# Revit family: Distributeur
name_source: partatom
category: Furniture
units: mm (PartAtom-declared; Revit-internal decimal feet)

## family parameters
Cut with Voids When Loaded = No
Host = Face
Room Calculation Point = No
Shared = No

## types (1)
- Distributeur
    Adresse = ZI de Chapotin BP 6 69970 Chaponnay FRANCE
    BIM object by Polantis = http://www.polantis.com
    Default Elevation = 100 cm
    Description = Fabricant Français d'Accessoires Sanitaires pour Collectivites, PELLET ASC a developpe des gammes specialisees pour ameliorer le Confort et la Securite de 

la salle de bain au quotidien.
    Fax. = 04.78.96.70.52
    Manufacturer = Pellet ASC
    Model = 003511 Distributeur papier WC en laiton nickelchrom- 152 96 68 mm avec rouleau bois18 mm
    Telephone = 04.78.96.82.20
    Type Comments = Confort, Securite et Hygiene
    URL = http://www.pellet-asc.fr
    m = Finish - CH

## geometry (parser evidence)
native form markers: Sweep x1
no freeform markers — native parametric forms only
